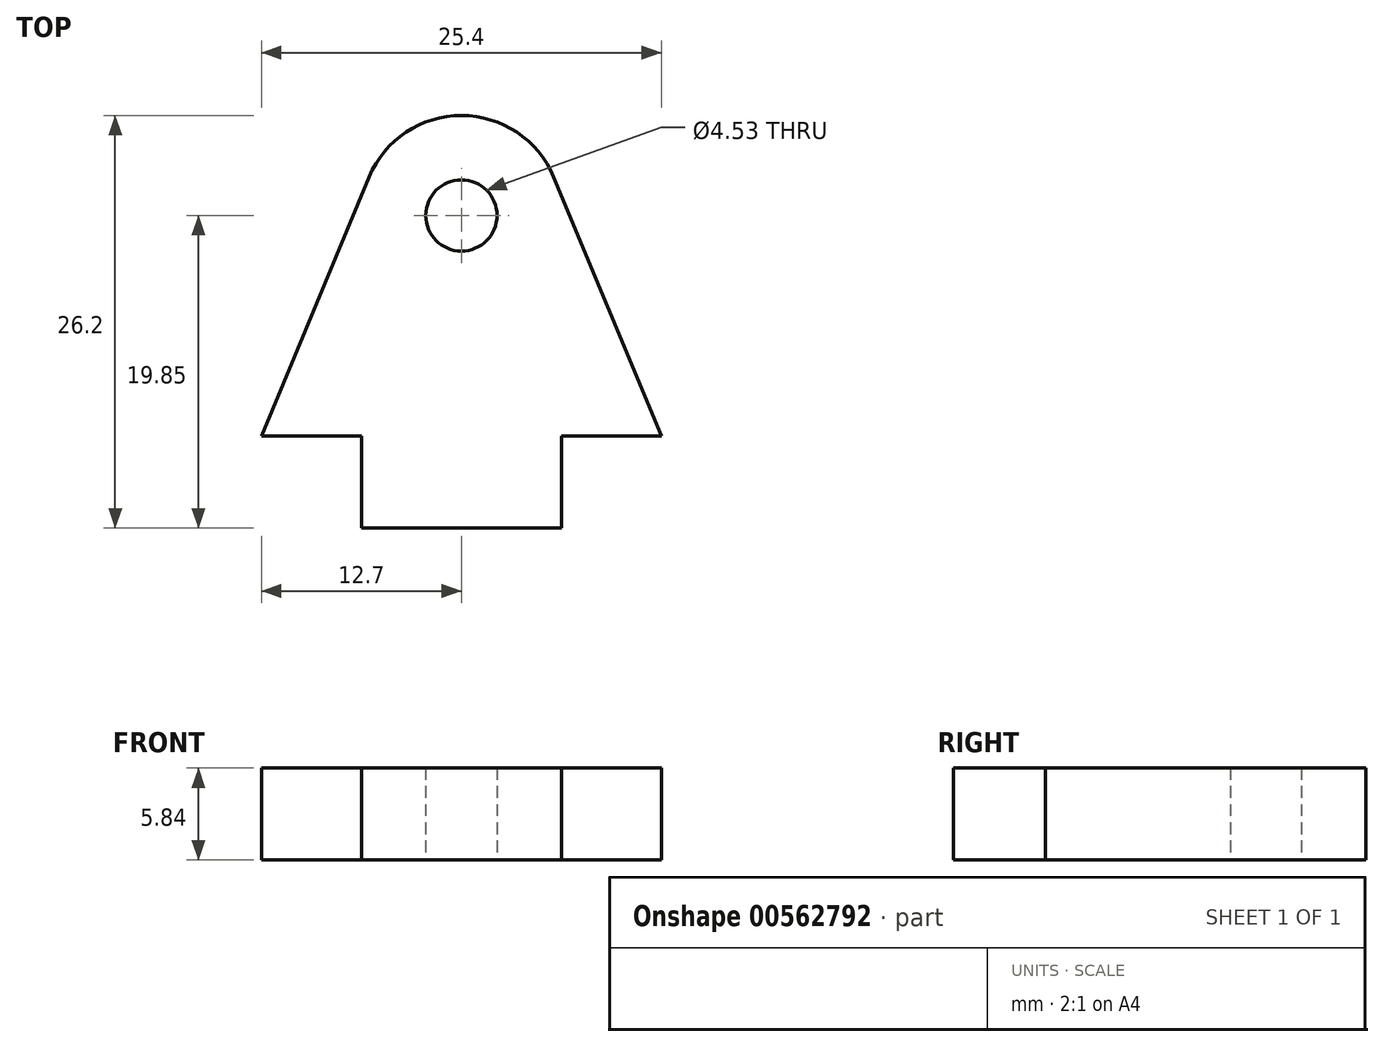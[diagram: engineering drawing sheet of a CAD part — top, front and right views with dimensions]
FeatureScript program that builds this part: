
annotation { "Feature Type Name" : "Feature", "Feature Type Description" : "" }
export const myFeature = defineFeature(function(context is Context, id is Id, definition is map)
    precondition{}
    {
        {
            var Q0;
            Q0=qCreatedBy(makeId("Top.planeOp"),FACE);
            var sketch = newSketch(context, id + "F0", { "sketchPlane" : qUnion([Q0])});
            skCircle(sketch, "E0", {"center": v(0, 0) * mm, "radius": 2.26 * mm});
            skLineSegment(sketch, "E1.top", {"start": v(-6.35, -19.85) * mm, "end": v(6.35, -19.85) * mm});
            skLineSegment(sketch, "E1.left", {"start": v(-6.35, -14) * mm, "end": v(-6.35, -19.85) * mm});
            skLineSegment(sketch, "E1.right", {"start": v(6.35, -14) * mm, "end": v(6.35, -19.85) * mm});
            skPoint(sketch, "E1.middle", {"position": v(0, -16.92) * mm});
            skArc(sketch, "E2", {"start": v(5.86, 2.44) * mm, "mid": v(0, 6.35) * mm, "end": v(-5.86, 2.44) * mm});
            skLineSegment(sketch, "E3", {"start": v(-6.35, -14) * mm, "end": v(-12.7, -14) * mm});
            skLineSegment(sketch, "E4", {"start": v(-12.7, -14) * mm, "end": v(-5.86, 2.44) * mm});
            skLineSegment(sketch, "E5.MirrorCS", {"start": v(12.7, -14) * mm, "end": v(5.86, 2.44) * mm});
            skLineSegment(sketch, "E6.MirrorCS", {"start": v(6.35, -14) * mm, "end": v(12.7, -14) * mm});
            skSolve(sketch);
        }
        {
            var Q0;
            Q0 = qSketchRegion(id + "F0", true);
            extrude(context, id + "F1", {"entities" : qUnion([Q0]), "depth" : 5.84 * mm, "offsetDistance" : 25.4 * mm});
        }
    });
